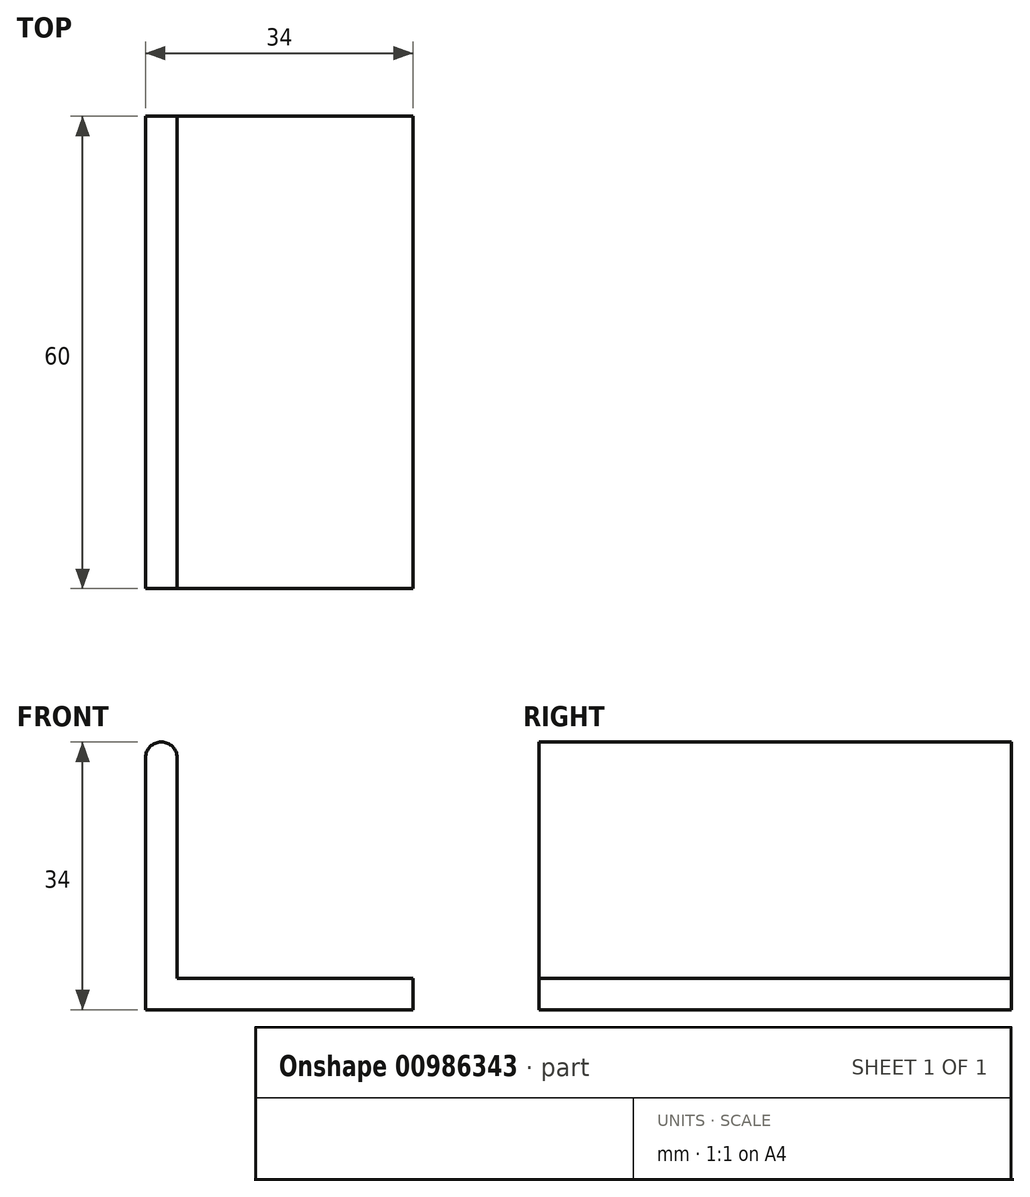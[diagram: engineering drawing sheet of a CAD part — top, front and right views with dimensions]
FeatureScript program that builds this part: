
annotation { "Feature Type Name" : "Feature", "Feature Type Description" : "" }
export const myFeature = defineFeature(function(context is Context, id is Id, definition is map)
    precondition{}
    {
        {
            var Q0;
            Q0=qCreatedBy(makeId("Front.planeOp"),FACE);
            var sketch = newSketch(context, id + "F0", { "sketchPlane" : qUnion([Q0])});
            skLineSegment(sketch, "E0", {"start": v(0, 0) * mm, "end": v(0, 34) * mm});
            skLineSegment(sketch, "E1", {"start": v(0, 0) * mm, "end": v(34, 0) * mm});
            skLineSegment(sketch, "E2", {"start": v(34, 0) * mm, "end": v(34, 4) * mm});
            skLineSegment(sketch, "E3", {"start": v(34, 4) * mm, "end": v(4, 4) * mm});
            skLineSegment(sketch, "E4", {"start": v(4, 4) * mm, "end": v(4, 34) * mm});
            skLineSegment(sketch, "E5", {"start": v(4, 34) * mm, "end": v(0, 34) * mm});
            skSolve(sketch);
        }
        {
            var Q0;
            Q0 = qSketchRegion(id + "F0", true);
            extrude(context, id + "F1", {"entities" : qUnion([Q0]), "depth" : 60 * mm, "offsetDistance" : 25 * mm});
        }
        {
            var Q0;
            Q0=makeQuery(id+"F1.opExtrude","SWEPT_EDGE",EDGE,{"disambiguationData":[OSD([sQuery(id+"F0.wireOp",EDGE,"E0"),sQuery(id+"F0.wireOp",EDGE,"E5")])]});
            var Q1;
            Q1=makeQuery(id+"F1.opExtrude","SWEPT_EDGE",EDGE,{"disambiguationData":[OSD([sQuery(id+"F0.wireOp",EDGE,"E4"),sQuery(id+"F0.wireOp",EDGE,"E5")])]});
            fillet(context, id + "F2", {"entities" : qUnion([Q0, Q1]), "radius" : 2 * mm, "tangentPropagation" : true, "allowEdgeOverflow" : false});
        }
    });
